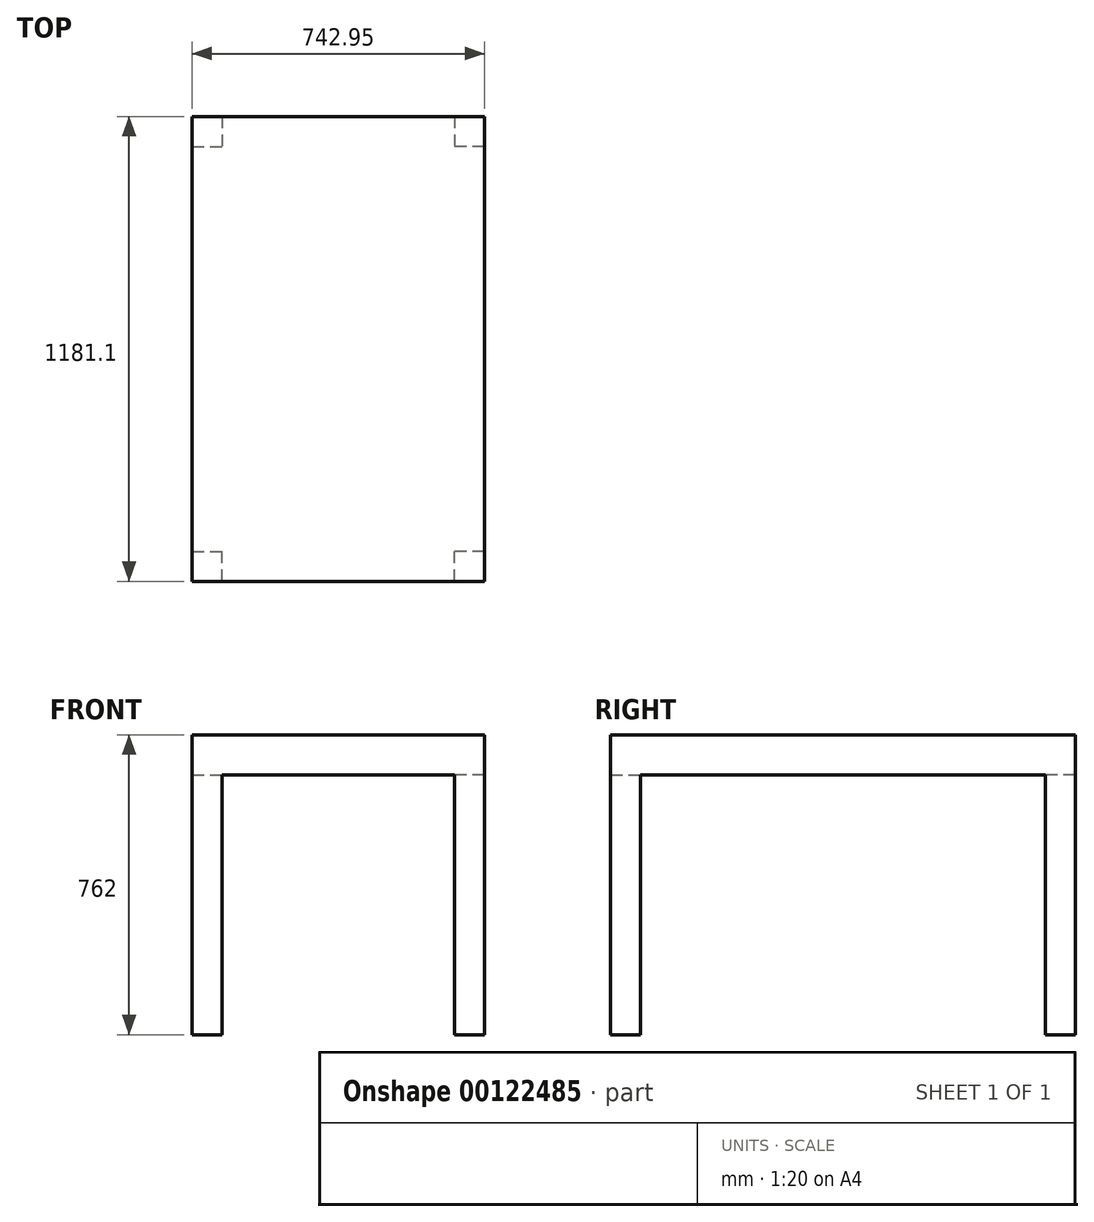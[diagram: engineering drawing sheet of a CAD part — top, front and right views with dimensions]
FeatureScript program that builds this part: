
annotation { "Feature Type Name" : "Feature", "Feature Type Description" : "" }
export const myFeature = defineFeature(function(context is Context, id is Id, definition is map)
    precondition{}
    {
        {
            var Q0;
            Q0=qCreatedBy(makeId("Top.planeOp"),FACE);
            var sketch = newSketch(context, id + "F0", { "sketchPlane" : qUnion([Q0])});
            skLineSegment(sketch, "E0.bottom", {"start": v(0, 0) * mm, "end": v(742.95, 0) * mm});
            skLineSegment(sketch, "E0.top", {"start": v(0, 1181.1) * mm, "end": v(742.95, 1181.1) * mm});
            skLineSegment(sketch, "E0.left", {"start": v(0, 0) * mm, "end": v(0, 1181.1) * mm});
            skLineSegment(sketch, "E0.right", {"start": v(742.95, 0) * mm, "end": v(742.95, 1181.1) * mm});
            skSolve(sketch);
        }
        {
            var Q0;
            Q0=qCreatedBy(makeId("Top.planeOp"),FACE);
            var sketch = newSketch(context, id + "F1", { "sketchPlane" : qUnion([Q0])});
            skLineSegment(sketch, "E1.bottom", {"start": v(0, 1181.1) * mm, "end": v(76.2, 1181.1) * mm});
            skLineSegment(sketch, "E1.top", {"start": v(0, 1104.9) * mm, "end": v(76.2, 1104.9) * mm});
            skLineSegment(sketch, "E1.left", {"start": v(0, 1181.1) * mm, "end": v(0, 1104.9) * mm});
            skLineSegment(sketch, "E1.right", {"start": v(76.2, 1181.1) * mm, "end": v(76.2, 1104.9) * mm});
            skLineSegment(sketch, "E2.bottom", {"start": v(742.95, 1181.1) * mm, "end": v(666.75, 1181.1) * mm});
            skLineSegment(sketch, "E2.top", {"start": v(742.95, 1104.9) * mm, "end": v(666.75, 1104.9) * mm});
            skLineSegment(sketch, "E2.left", {"start": v(742.95, 1181.1) * mm, "end": v(742.95, 1104.9) * mm});
            skLineSegment(sketch, "E2.right", {"start": v(666.75, 1181.1) * mm, "end": v(666.75, 1104.9) * mm});
            skLineSegment(sketch, "E3.bottom", {"start": v(742.95, 0) * mm, "end": v(666.75, 0) * mm});
            skLineSegment(sketch, "E3.top", {"start": v(742.95, 76.2) * mm, "end": v(666.75, 76.2) * mm});
            skLineSegment(sketch, "E3.left", {"start": v(742.95, 0) * mm, "end": v(742.95, 76.2) * mm});
            skLineSegment(sketch, "E3.right", {"start": v(666.75, 0) * mm, "end": v(666.75, 76.2) * mm});
            skLineSegment(sketch, "E4.bottom", {"start": v(0, 0) * mm, "end": v(76.2, 0) * mm});
            skLineSegment(sketch, "E4.top", {"start": v(0, 76.2) * mm, "end": v(76.2, 76.2) * mm});
            skLineSegment(sketch, "E4.left", {"start": v(0, 0) * mm, "end": v(0, 76.2) * mm});
            skLineSegment(sketch, "E4.right", {"start": v(76.2, 0) * mm, "end": v(76.2, 76.2) * mm});
            skSolve(sketch);
        }
        {
            var Q0;
            Q0 = qSketchRegion(id + "F0", true);
            extrude(context, id + "F2", {"entities" : qUnion([Q0]), "oppositeDirection" : true, "depth" : 101.6 * mm});
        }
        {
            var Q0;
            Q0 = qSketchRegion(id + "F1", true);
            extrude(context, id + "F3", {"entities" : qUnion([Q0]), "operationType" : NewBodyOperationType.ADD, "oppositeDirection" : true, "depth" : 762 * mm});
        }
    });
